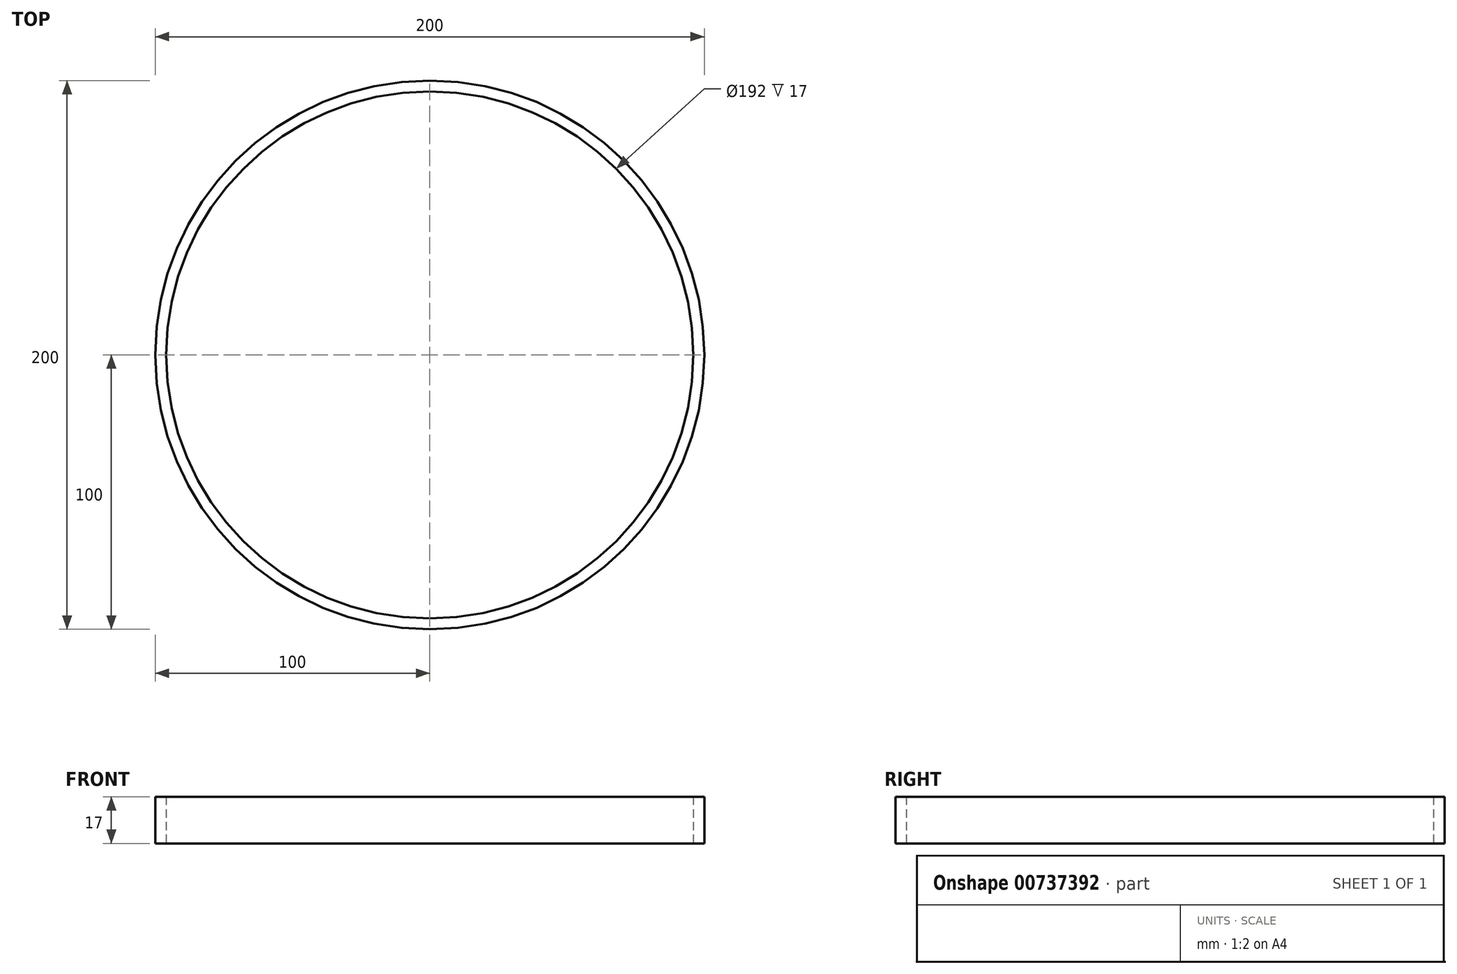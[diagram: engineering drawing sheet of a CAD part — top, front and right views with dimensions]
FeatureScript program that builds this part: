
annotation { "Feature Type Name" : "Feature", "Feature Type Description" : "" }
export const myFeature = defineFeature(function(context is Context, id is Id, definition is map)
    precondition{}
    {
        {
            var Q0;
            Q0=qCreatedBy(makeId("Top.planeOp"),FACE);
            var sketch = newSketch(context, id + "F0", { "sketchPlane" : qUnion([Q0])});
            skCircle(sketch, "E0", {"center": v(0, 0) * mm, "radius": 100 * mm});
            skCircle(sketch, "E1.0", {"center": v(0, 0) * mm, "radius": 96 * mm});
            skSolve(sketch);
        }
        {
            var Q0;
            Q0 = qSketchRegion(id + "F0", true);
            extrude(context, id + "F1", {"entities" : qUnion([Q0]), "depth" : 17 * mm, "offsetDistance" : 25 * mm});
        }
    });
